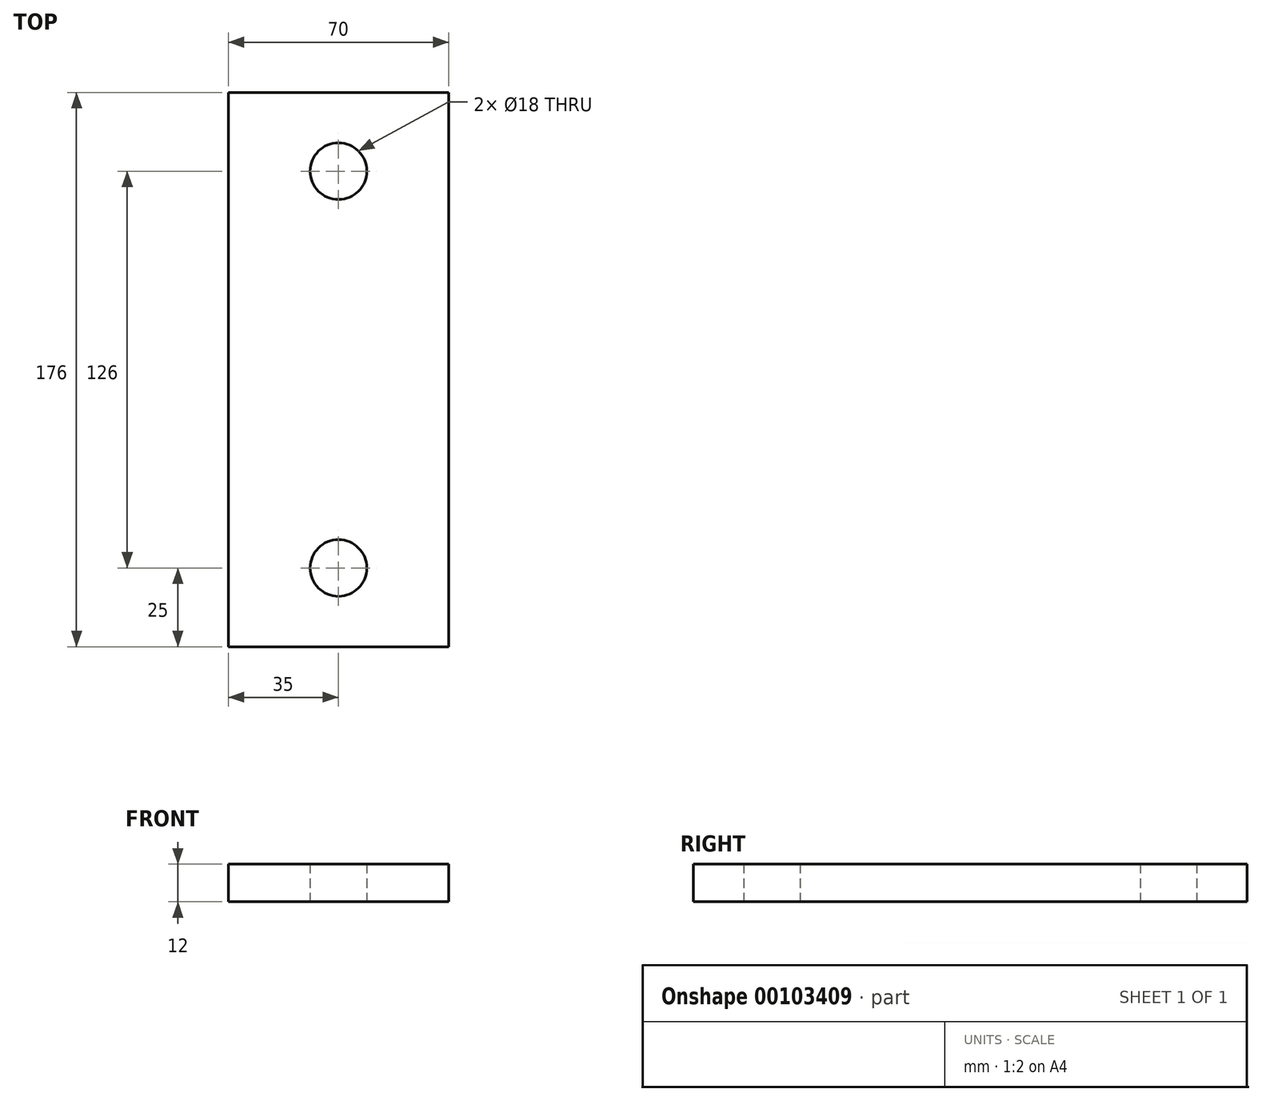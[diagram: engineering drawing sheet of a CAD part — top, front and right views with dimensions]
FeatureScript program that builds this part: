
annotation { "Feature Type Name" : "Feature", "Feature Type Description" : "" }
export const myFeature = defineFeature(function(context is Context, id is Id, definition is map)
    precondition{}
    {
        {
            var Q0;
            Q0=qCreatedBy(makeId("Top.planeOp"),FACE);
            var sketch = newSketch(context, id + "F0", { "sketchPlane" : qUnion([Q0])});
            skLineSegment(sketch, "E0.bottom", {"start": v(-35, 88) * mm, "end": v(35, 88) * mm});
            skLineSegment(sketch, "E0.top", {"start": v(-35, -88) * mm, "end": v(35, -88) * mm});
            skLineSegment(sketch, "E0.left", {"start": v(-35, 88) * mm, "end": v(-35, -88) * mm});
            skLineSegment(sketch, "E0.right", {"start": v(35, 88) * mm, "end": v(35, -88) * mm});
            skPoint(sketch, "E1", {"position": v(-35, 0) * mm});
            skPoint(sketch, "E2", {"position": v(0, -88) * mm});
            skSolve(sketch);
        }
        {
            var Q0;
            Q0 = qSketchRegion(id + "F0", true);
            extrude(context, id + "F1", {"entities" : qUnion([Q0]), "depth" : 12 * mm, "offsetDistance" : 25 * mm});
        }
        {
            var Q0;
            Q0=makeQuery(id+"F1.opExtrude","CAP_FACE",FACE,{"disambiguationData":[OSD([sQuery(id+"F0.wireOp",EDGE,"E0.bottom"),sQuery(id+"F0.wireOp",EDGE,"E0.top"),sQuery(id+"F0.wireOp",EDGE,"E0.left"),sQuery(id+"F0.wireOp",EDGE,"E0.right")])],"isStart":true});
            var sketch = newSketch(context, id + "F2", { "sketchPlane" : qUnion([Q0])});
            skCircle(sketch, "E3", {"center": v(0, 63) * mm, "radius": 9 * mm});
            skCircle(sketch, "E4", {"center": v(0, -63) * mm, "radius": 9 * mm});
            skSolve(sketch);
        }
        {
            var Q0;
            Q0 = qSketchRegion(id + "F2", true);
            extrude(context, id + "F3", {"entities" : qUnion([Q0]), "operationType" : NewBodyOperationType.REMOVE, "oppositeDirection" : true, "depth" : 25 * mm, "offsetDistance" : 25 * mm});
        }
        {
            var Q0;
            Q0=makeQuery(id+"F1.opExtrude","CAP_FACE",FACE,{"disambiguationData":[OSD([sQuery(id+"F0.wireOp",EDGE,"E0.bottom"),sQuery(id+"F0.wireOp",EDGE,"E0.top"),sQuery(id+"F0.wireOp",EDGE,"E0.left"),sQuery(id+"F0.wireOp",EDGE,"E0.right")])],"isStart":false});
            var sketch = newSketch(context, id + "F4", { "sketchPlane" : qUnion([Q0])});
            skLineSegment(sketch, "E5", {"start": v(0, -63) * mm, "end": v(0, 63) * mm});
            skPoint(sketch, "E6", {"position": v(0, 0) * mm});
            skPoint(sketch, "E7", {"position": v(0, -18) * mm});
            skSolve(sketch);
        }
    });
